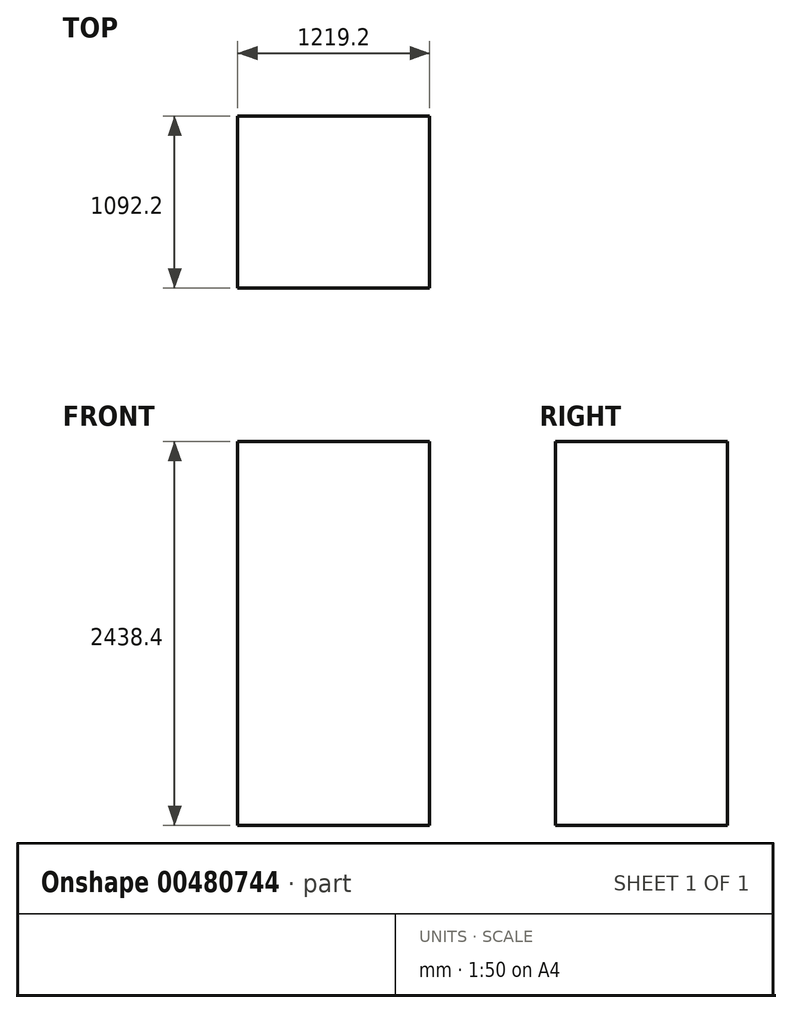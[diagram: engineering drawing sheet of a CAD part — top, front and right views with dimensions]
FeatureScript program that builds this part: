
annotation { "Feature Type Name" : "Feature", "Feature Type Description" : "" }
export const myFeature = defineFeature(function(context is Context, id is Id, definition is map)
    precondition{}
    {
        {
            var Q0;
            Q0=qCreatedBy(makeId("Top.planeOp"),FACE);
            var sketch = newSketch(context, id + "F0", { "sketchPlane" : qUnion([Q0])});
            skLineSegment(sketch, "E0.bottom", {"start": v(609.6, 546.1) * mm, "end": v(-609.6, 546.1) * mm});
            skLineSegment(sketch, "E0.top", {"start": v(609.6, -546.1) * mm, "end": v(-609.6, -546.1) * mm});
            skLineSegment(sketch, "E0.left", {"start": v(609.6, 546.1) * mm, "end": v(609.6, -546.1) * mm});
            skLineSegment(sketch, "E0.right", {"start": v(-609.6, 546.1) * mm, "end": v(-609.6, -546.1) * mm});
            skPoint(sketch, "E0.middle", {"position": v(0, 0) * mm});
            skSolve(sketch);
        }
        {
            var Q0;
            Q0=makeQuery(id+"F0.imprint","IMPRINT",FACE,{"disambiguationData":[TD([[makeQuery(id+"F0.imprint","IMPRINT",EDGE,{"derivedFrom":sQuery(id+"F0.wireOp",EDGE,"E0.bottom")}),1.0]])]});
            extrude(context, id + "F1", {"entities" : qUnion([Q0]), "depth" : 2438.4 * mm});
        }
    });
